# Revit family: ERA_LF_CS_SPL-510
name_source: partatom
category: Осветительные приборы
units: mm (PartAtom-declared; Revit-internal decimal feet)

## family parameters
Всегда вертикально = Да
Заголовок OmniClass = Lighting
Источник света = Да
На основе рабочей плоскости = Нет
Номер OmniClass = 23.80.70.00
Общий = Нет
При загрузке вырезать с полостями = Нет
Размер круглого соединителя = Использовать диаметр
Тип детали = Нормальный
Точка расчета площади = Да

## types (4) — shared parameters
ADSK_Единица измерения = шт.
ADSK_Завод-изготовитель = ЭРА
ADSK_Классификация нагрузок = Освещение
ADSK_Количество фаз = 1
ADSK_Коэффициент мощности = 0.95
ADSK_Масса = 1.675
ADSK_Наименование краткое = Светильник
ADSK_Напряжение = 230 В
ADSK_Номинальная мощность = 40 Вт
ADSK_Полная мощность = 42 В·А
ADSK_Примечание = Внешний AC/DC драйвер с гальванической развязкой, поликарбонат
ADSK_Размер_Высота = 8 мм
ADSK_Размер_Длина = 595 мм
ADSK_Размер_Ширина = 595 мм
URL = https://www.eraworld.ru
_Корпус_Высота = 8 мм
_Корпус_Диаметр = 1 мм
_Корпус_Длина = 595 мм
_Корпус_Ширина = 595 мм
_УГО_Диаметр = 5.95 мм
_УГО_Длина = 5.95 мм
_УГО_Ширина = 5.95 мм
Видимая форма излучения при визуализации = Нет
Геометрия изделия = Квадратный
Излучение по длине прямоугольника = 595 мм
Излучение по ширине прямоугольника = 595 мм
Источник света = LED
Класс защиты = III
Класс пожароопасности = Нет
Комплект = Внешний AC/DC драйвер с гальванической развязкой
Разработчик модели = https://www.teslabim.ru
Светофильтр = 16777215
Смещение цветовой температуры при затухании лампы = <Нет>
Степень защиты IP = IP40
Тип установки = Потолочный
УГО_Масштаб = 100
Угол наклона = 90,00°
Цвет = Белый
zero-valued in all types: ADSK_Размер_Диаметр

## per-type parameters (varying)
| type | ADSK_Марка | ADSK_Наименование | ADSK_Обозначение | Файл фотометрической сетки |
| SPL-510-S-40K-040, LED, IP40, 595х595х8 мм (ДхШхВ), 40 Вт, 4000 К, 3420 лм, класс защиты III, в комплекте (внешний ac/dc драйвер с гальванической развязкой) | SPL-510-S-40K-040 | Светильник, LED, квадратный, потолочный, IP40, 595х595х8 мм (ДхШхВ), 40 Вт, 4000 К, 3420 лм, класс защиты III, в комплекте (внешний ac/dc драйвер с гальванической развязкой) | SPL-510-S-40K-040 | SPL-510-S-40K-040.ies |
| SPL-510-S-65K-040, LED, IP40, 595х595х8 мм (ДхШхВ), 40 Вт, 6500 К, 3420 лм, класс защиты III, в комплекте (внешний ac/dc драйвер с гальванической развязкой) | SPL-510-S-65K-040 | Светильник, LED, квадратный, потолочный, IP40, 595х595х8 мм (ДхШхВ), 40 Вт, 6500 К, 3420 лм, класс защиты III, в комплекте (внешний ac/dc драйвер с гальванической развязкой) | SPL-510-S-65K-040 | SPL-510-S-65K-040.ies |
| SPL-510-W-40K-040, LED, IP40, 595х595х8 мм (ДхШхВ), 40 Вт, 4000 К, 3420 лм, класс защиты III, в комплекте (внешний ac/dc драйвер с гальванической развязкой) | SPL-510-W-40K-040 | Светильник, LED, квадратный, потолочный, IP40, 595х595х8 мм (ДхШхВ), 40 Вт, 4000 К, 3420 лм, класс защиты III, в комплекте (внешний ac/dc драйвер с гальванической развязкой) | SPL-510-W-40K-040 | SPL-510-W-40K-040.ies |
| SPL-510-W-65K-040, LED, IP40, 595х595х8 мм (ДхШхВ), 40 Вт, 6500 К, 3420 лм, класс защиты III, в комплекте (внешний ac/dc драйвер с гальванической развязкой) | SPL-510-W-65K-040 | Светильник, LED, квадратный, потолочный, IP40, 595х595х8 мм (ДхШхВ), 40 Вт, 6500 К, 3420 лм, класс защиты III, в комплекте (внешний ac/dc драйвер с гальванической развязкой) | SPL-510-W-65K-040 | SPL-510-W-65K-040.ies |
